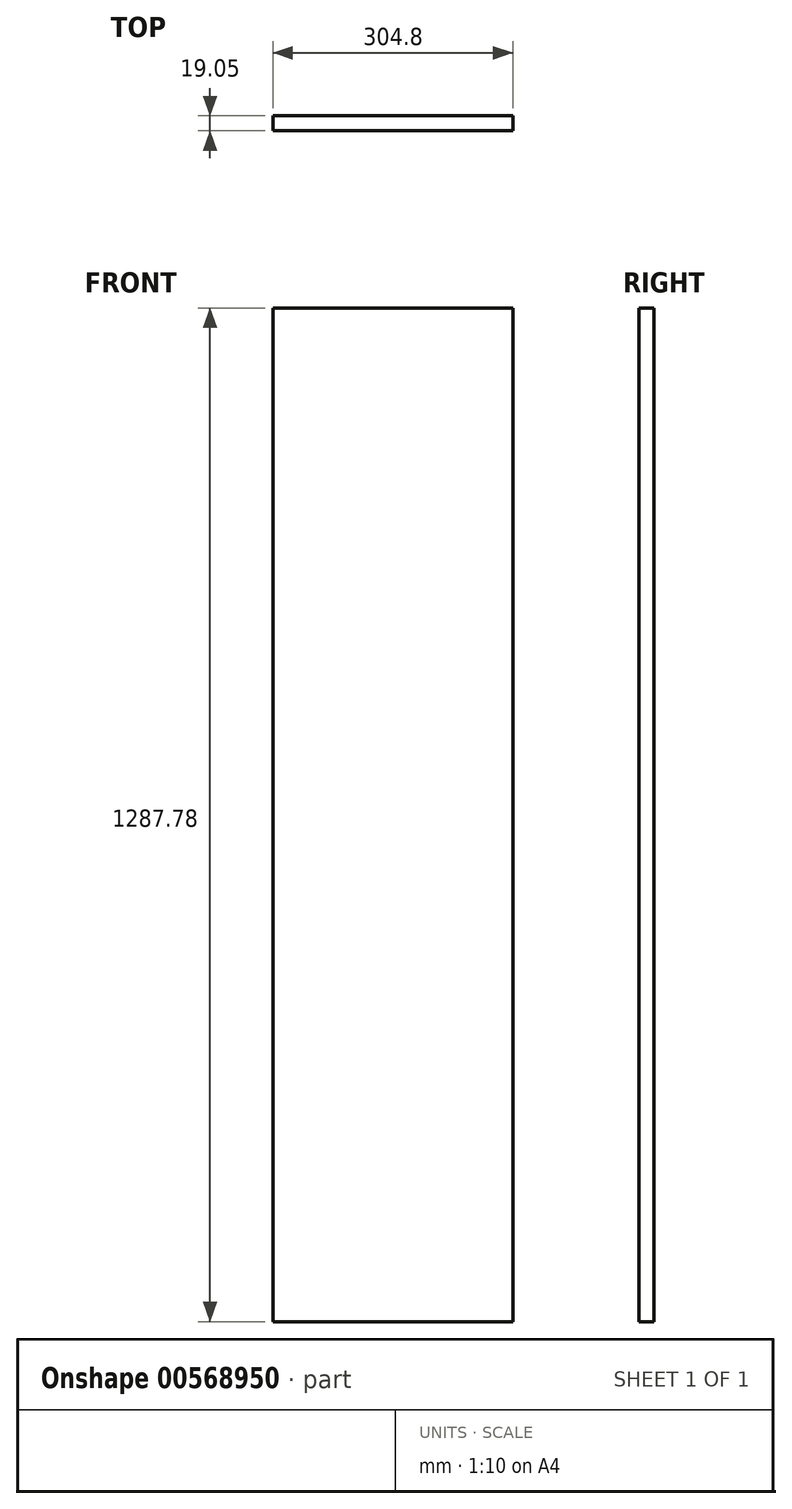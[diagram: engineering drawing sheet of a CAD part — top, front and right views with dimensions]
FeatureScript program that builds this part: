
annotation { "Feature Type Name" : "Feature", "Feature Type Description" : "" }
export const myFeature = defineFeature(function(context is Context, id is Id, definition is map)
    precondition{}
    {
        {
            var Q0;
            Q0=qCreatedBy(makeId("Front.planeOp"),FACE);
            var sketch = newSketch(context, id + "F0", { "sketchPlane" : qUnion([Q0])});
            skLineSegment(sketch, "E0.bottom", {"start": v(-173.64, 1235.41) * mm, "end": v(131.16, 1235.41) * mm});
            skLineSegment(sketch, "E0.top", {"start": v(-173.64, -52.37) * mm, "end": v(131.16, -52.37) * mm});
            skLineSegment(sketch, "E0.left", {"start": v(-173.64, 1235.41) * mm, "end": v(-173.64, -52.37) * mm});
            skLineSegment(sketch, "E0.right", {"start": v(131.16, 1235.41) * mm, "end": v(131.16, -52.37) * mm});
            skSolve(sketch);
        }
        {
            var Q0;
            Q0 = qSketchRegion(id + "F0", true);
            extrude(context, id + "F1", {"entities" : qUnion([Q0]), "depth" : 19.05 * mm, "offsetDistance" : 25.4 * mm});
        }
    });
